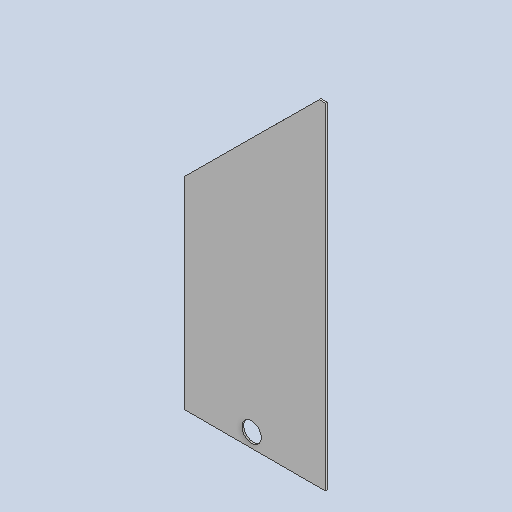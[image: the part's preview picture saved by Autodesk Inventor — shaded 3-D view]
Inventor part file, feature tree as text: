
AUTODESK INVENTOR PART (.ipt)
format: ipt  version: 2025 (Build 290162010, 162A)  size: 220,160 bytes
history: native  units: mm
features: extrude x3, sketch x2, fillet x1, pattern_circular x1, projected_geometry x1, other x1
ambient origin geometry x8: Origin, YZ Plane, XZ Plane, XY Plane, X Axis, Y Axis, Z Axis, Center Point
bodies: Solid1 (feature_tree)
feature tree (9):
  extrude  "Extrusion1"  Depth=1180.0mm
  fillet  "Fillet1"  Radius=1180.0mm
  extrude  "Extrusion4"  Depth=10.0mm
  pattern_circular  "Circular Pattern3"  Count=191  [1 undecoded]
  extrude  "Extrusion5"  [1 undecoded]
  sketch  "Sketch4"  dims[d1=840.0mm d3=1150.0mm d12=1180.0mm]
  sketch  "Sketch5"  dims[d13=950.0mm d14=111.0mm d15=1910.0mm d17=-521.637743mm d18=377.0mm d19=-269.216713mm d24=10.0mm d25=0.0mm d34=380.0mm d35=80.0mm d37=2140.0mm d52=530.0mm d53=5.0mm d54=10.0mm d55=30.0mm d56=10.0mm d59=265.0mm d60=13.0mm d61=1.963495mm d62=10.0mm d63=0.0mm d64=160.0mm d65=360.0deg d67=5.0mm d68=5.0mm d69=780.0mm d71=1078.0mm d72=340.0mm d73=1340.0mm d74=0.0mm d75=0.0mm d70=0.872665mm]
  projected_geometry  "Projected Loop1"
  other  "Definition1"
note: 2 required parameter values undecoded (feature->parameter linkage not recoverable at this tier; creation-order binding heuristic only, values carry confidence <= 0.55)
